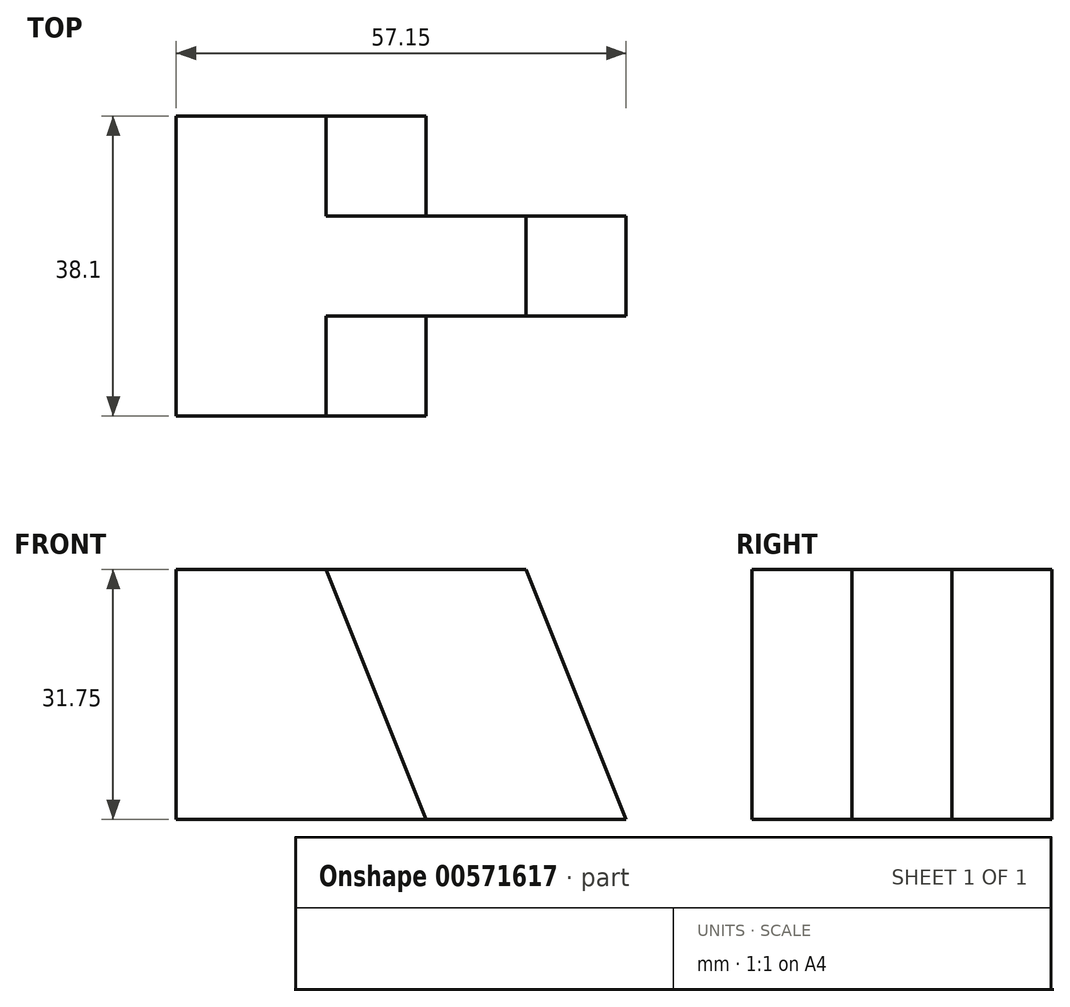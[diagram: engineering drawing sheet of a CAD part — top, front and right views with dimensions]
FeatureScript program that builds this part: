
annotation { "Feature Type Name" : "Feature", "Feature Type Description" : "" }
export const myFeature = defineFeature(function(context is Context, id is Id, definition is map)
    precondition{}
    {
        {
            var Q0;
            Q0=qCreatedBy(makeId("Front.planeOp"),FACE);
            var sketch = newSketch(context, id + "F0", { "sketchPlane" : qUnion([Q0])});
            skLineSegment(sketch, "E0", {"start": v(0, 0) * mm, "end": v(57.15, 0) * mm});
            skLineSegment(sketch, "E1", {"start": v(0, 0) * mm, "end": v(0, 31.75) * mm});
            skLineSegment(sketch, "E2", {"start": v(0, 31.75) * mm, "end": v(44.45, 31.75) * mm});
            skLineSegment(sketch, "E3", {"start": v(44.45, 31.75) * mm, "end": v(57.15, 0) * mm});
            skSolve(sketch);
        }
        {
            var Q0;
            Q0 = qSketchRegion(id + "F0", true);
            extrude(context, id + "F1", {"entities" : qUnion([Q0]), "depth" : 12.7 * mm, "offsetDistance" : 25.4 * mm});
        }
        {
            var Q0;
            Q0=qCreatedBy(makeId("Front.planeOp"),FACE);
            var sketch = newSketch(context, id + "F2", { "sketchPlane" : qUnion([Q0])});
            skLineSegment(sketch, "E4", {"start": v(0, 0) * mm, "end": v(31.75, 0) * mm});
            skLineSegment(sketch, "E5", {"start": v(0, 0) * mm, "end": v(0, 31.75) * mm});
            skLineSegment(sketch, "E6", {"start": v(0, 31.75) * mm, "end": v(19.05, 31.75) * mm});
            skLineSegment(sketch, "E7", {"start": v(19.05, 31.75) * mm, "end": v(31.75, 0) * mm});
            skSolve(sketch);
        }
        {
            var Q0;
            Q0 = qSketchRegion(id + "F2", true);
            extrude(context, id + "F3", {"entities" : qUnion([Q0]), "operationType" : NewBodyOperationType.ADD, "depth" : 25.4 * mm, "offsetDistance" : 25.4 * mm});
        }
        {
            var Q0;
            Q0=qCreatedBy(makeId("Front.planeOp"),FACE);
            var sketch = newSketch(context, id + "F4", { "sketchPlane" : qUnion([Q0])});
            skLineSegment(sketch, "E8", {"start": v(0, 0) * mm, "end": v(0, 31.75) * mm});
            skLineSegment(sketch, "E9", {"start": v(0, 31.75) * mm, "end": v(19.05, 31.75) * mm});
            skLineSegment(sketch, "E10", {"start": v(0, 0) * mm, "end": v(31.75, 0) * mm});
            skLineSegment(sketch, "E11", {"start": v(31.75, 0) * mm, "end": v(19.05, 31.75) * mm});
            skSolve(sketch);
        }
        {
            var Q0;
            Q0 = qSketchRegion(id + "F4", true);
            extrude(context, id + "F5", {"entities" : qUnion([Q0]), "operationType" : NewBodyOperationType.ADD, "oppositeDirection" : true, "depth" : 12.7 * mm, "offsetDistance" : 25.4 * mm});
        }
    });
